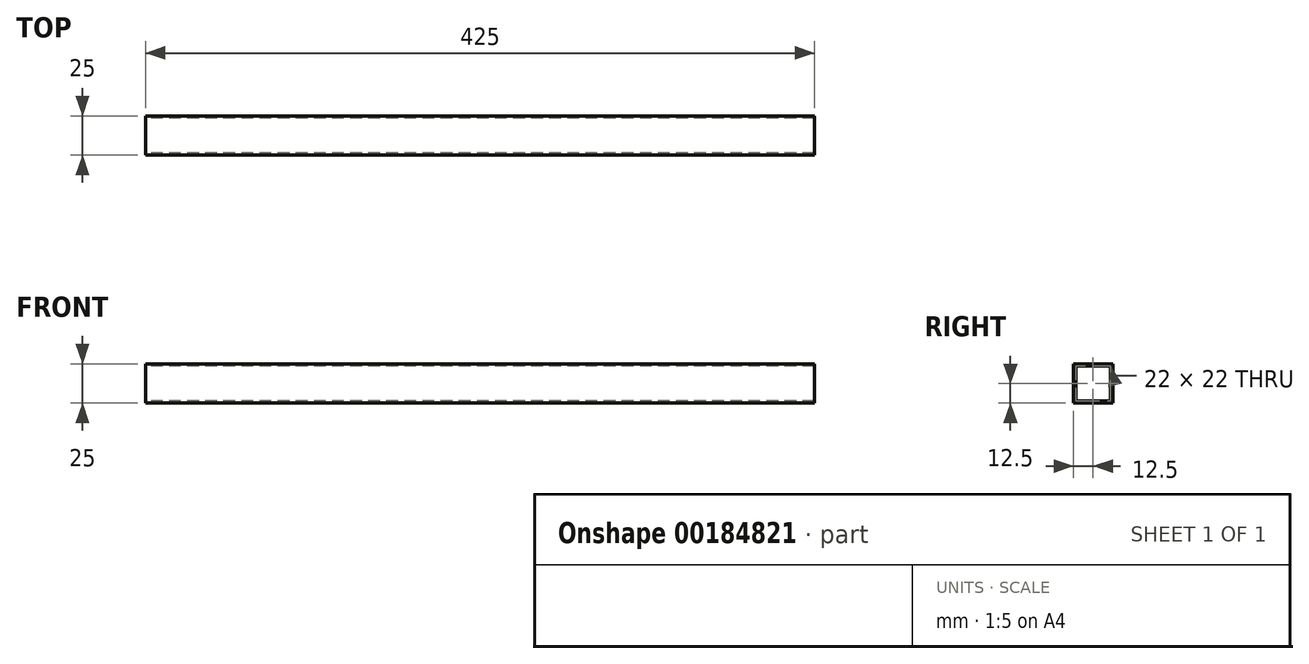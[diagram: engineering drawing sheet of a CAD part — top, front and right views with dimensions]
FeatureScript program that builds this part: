
annotation { "Feature Type Name" : "Feature", "Feature Type Description" : "" }
export const myFeature = defineFeature(function(context is Context, id is Id, definition is map)
    precondition{}
    {
        {
            var Q0;
            Q0=qCreatedBy(makeId("Right.planeOp"),FACE);
            var sketch = newSketch(context, id + "F0", { "sketchPlane" : qUnion([Q0])});
            skLineSegment(sketch, "E0.bottom", {"start": v(12.5, 12.5) * mm, "end": v(-12.5, 12.5) * mm});
            skLineSegment(sketch, "E0.top", {"start": v(12.5, -12.5) * mm, "end": v(-12.5, -12.5) * mm});
            skLineSegment(sketch, "E0.left", {"start": v(12.5, 12.5) * mm, "end": v(12.5, -12.5) * mm});
            skLineSegment(sketch, "E0.right", {"start": v(-12.5, 12.5) * mm, "end": v(-12.5, -12.5) * mm});
            skPoint(sketch, "E0.middle", {"position": v(0, 0) * mm});
            skSolve(sketch);
        }
        {
            var Q0;
            Q0=qSketchRegion(id+"F0",true);
            extrude(context, id + "F1", {"entities" : qUnion([Q0]), "depth" : 425 * mm});
        }
        {
            var Q0;
            Q0=qCreatedBy(makeId("Front.planeOp"),FACE);
            var sketch = newSketch(context, id + "F2", { "sketchPlane" : qUnion([Q0])});
            skLineSegment(sketch, "E1", {"start": v(0, 12.6) * mm, "end": v(35.35, -22.75) * mm});
            skLineSegment(sketch, "E2", {"start": v(425, 12.5) * mm, "end": v(395.64, -16.86) * mm});
            skLineSegment(sketch, "E3", {"start": v(0, 12.6) * mm, "end": v(0, -26.69) * mm});
            skLineSegment(sketch, "E4", {"start": v(0, -26.69) * mm, "end": v(35.35, -22.75) * mm});
            skLineSegment(sketch, "E5", {"start": v(425, 12.5) * mm, "end": v(425, -22.75) * mm});
            skLineSegment(sketch, "E6", {"start": v(425, -22.75) * mm, "end": v(395.64, -16.86) * mm});
            skSolve(sketch);
        }
        {
            var Q0;
            Q0=qCreatedBy(makeId("Right.planeOp"),FACE);
            var sketch = newSketch(context, id + "F3", { "sketchPlane" : qUnion([Q0])});
            skLineSegment(sketch, "E7.bottom", {"start": v(-11, 11) * mm, "end": v(11, 11) * mm});
            skLineSegment(sketch, "E7.top", {"start": v(-11, -11) * mm, "end": v(11, -11) * mm});
            skLineSegment(sketch, "E7.left", {"start": v(-11, 11) * mm, "end": v(-11, -11) * mm});
            skLineSegment(sketch, "E7.right", {"start": v(11, 11) * mm, "end": v(11, -11) * mm});
            skPoint(sketch, "E7.middle", {"position": v(0, 0) * mm});
            skSolve(sketch);
        }
        {
            var Q0;
            Q0=makeQuery(id+"F3.imprint","IMPRINT",FACE,{"disambiguationData":[TD([[makeQuery(id+"F3.imprint","IMPRINT",EDGE,{"derivedFrom":sQuery(id+"F3.wireOp",EDGE,"E7.bottom")}),-1.0]])]});
            var Q1;
            Q1=makeQuery(id+"F7keTeLZR2YRc63_1.boolean.opBoolean","COPY",FACE,{"derivedFrom":makeQuery(id+"F7keTeLZR2YRc63_1.opExtrude","SWEPT_FACE",FACE,{"disambiguationData":[OSD([sQuery(id+"F2.wireOp",EDGE,"E2")])]})});
            extrude(context, id + "F4", {"entities" : qUnion([Q0]), "operationType" : NewBodyOperationType.REMOVE, "endBound" : BoundingType.THROUGH_ALL, "endBoundEntityFace" : qUnion([Q1]), "depth" : 750 * mm});
        }
    });
